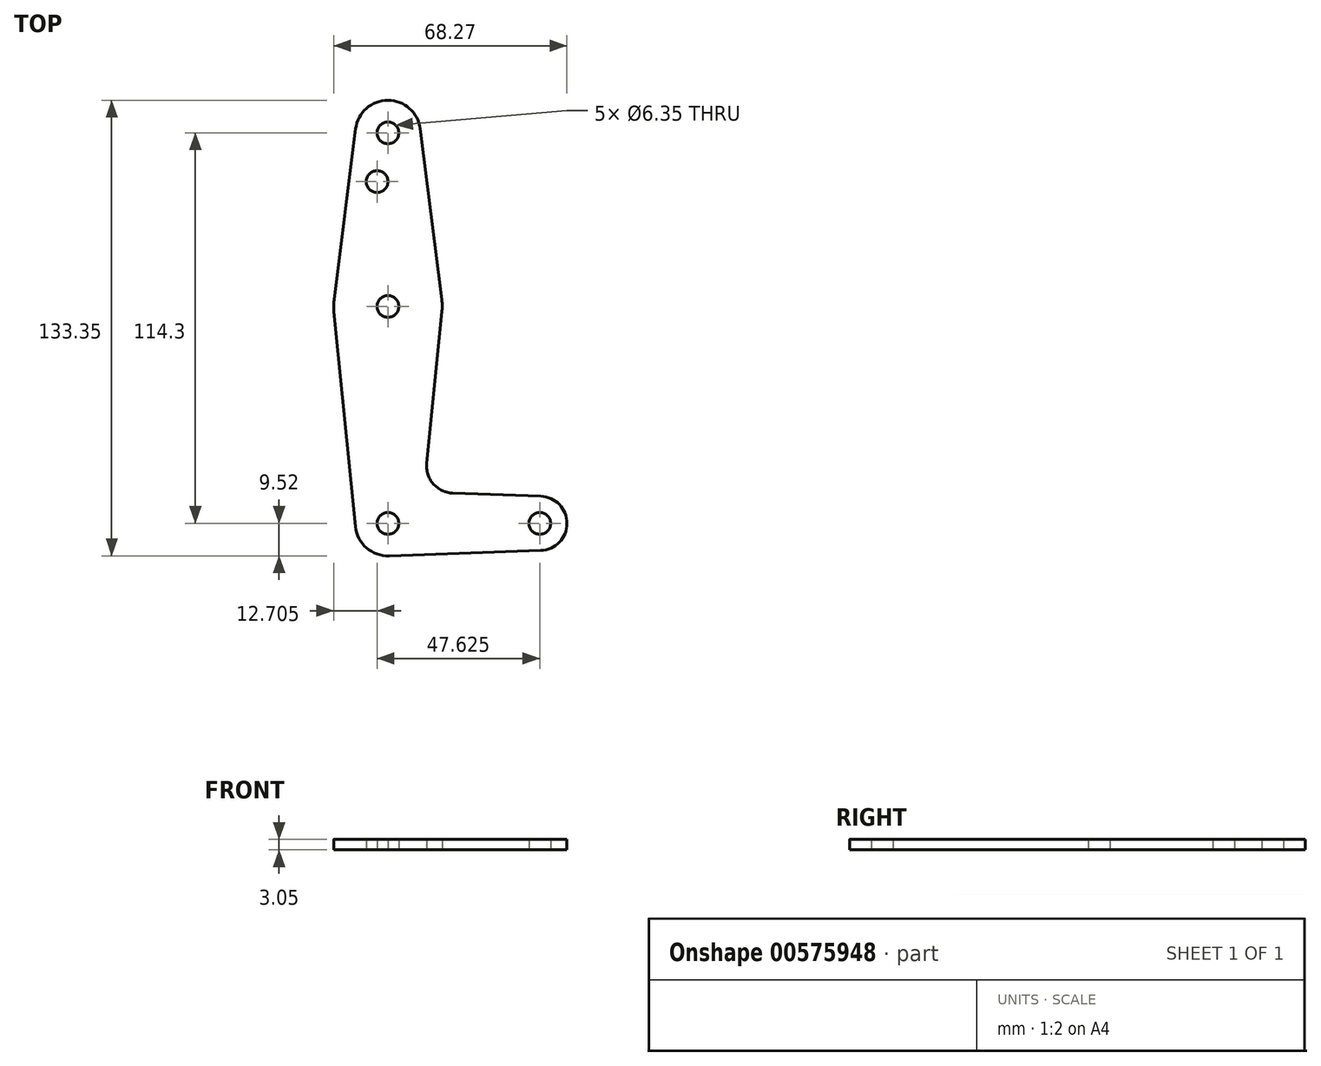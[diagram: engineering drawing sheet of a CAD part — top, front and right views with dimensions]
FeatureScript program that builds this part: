
annotation { "Feature Type Name" : "Feature", "Feature Type Description" : "" }
export const myFeature = defineFeature(function(context is Context, id is Id, definition is map)
    precondition{}
    {
        {
            var Q0;
            Q0=qCreatedBy(makeId("Top.planeOp"),FACE);
            var sketch = newSketch(context, id + "F0", { "sketchPlane" : qUnion([Q0])});
            skLineSegment(sketch, "E0", {"start": v(0, 0) * mm, "end": v(0, 114.3) * mm, "construction": true});
            skLineSegment(sketch, "E1", {"start": v(0, 0) * mm, "end": v(44.45, 0) * mm, "construction": true});
            skCircle(sketch, "E2", {"center": v(0, 114.3) * mm, "radius": 9.53 * mm});
            skCircle(sketch, "E3", {"center": v(0, 0) * mm, "radius": 9.53 * mm});
            skCircle(sketch, "E4", {"center": v(44.45, 0) * mm, "radius": 7.94 * mm});
            skCircle(sketch, "E5", {"center": v(0, 63.5) * mm, "radius": 15.88 * mm});
            skLineSegment(sketch, "E6", {"start": v(-15.75, 65.48) * mm, "end": v(-9.45, 115.5) * mm});
            skLineSegment(sketch, "E7", {"start": v(9.45, 115.5) * mm, "end": v(15.75, 65.48) * mm});
            skLineSegment(sketch, "E8", {"start": v(-15.8, 61.91) * mm, "end": v(-9.48, -0.95) * mm});
            skLineSegment(sketch, "E9", {"start": v(11.34, 17.6) * mm, "end": v(15.8, 61.91) * mm});
            skLineSegment(sketch, "E10", {"start": v(0.34, -9.52) * mm, "end": v(44.73, -7.93) * mm});
            skLineSegment(sketch, "E11", {"start": v(18.97, 8.85) * mm, "end": v(44.73, 7.93) * mm});
            skArc(sketch, "E12.filletArc", {"start": v(11.34, 17.6) * mm, "mid": v(13.26, 11.57) * mm, "end": v(18.97, 8.85) * mm});
            skCircle(sketch, "E13", {"center": v(0, 114.3) * mm, "radius": 3.18 * mm});
            skCircle(sketch, "E14", {"center": v(-3.18, 100.03) * mm, "radius": 3.18 * mm});
            skCircle(sketch, "E15", {"center": v(0, 63.5) * mm, "radius": 3.18 * mm});
            skCircle(sketch, "E16", {"center": v(0, 0) * mm, "radius": 3.18 * mm});
            skCircle(sketch, "E17", {"center": v(44.45, 0) * mm, "radius": 3.18 * mm});
            skSolve(sketch);
        }
        {
            var Q0;
            Q0 = qSketchRegion(id + "F0", true);
            extrude(context, id + "F1", {"entities" : qUnion([Q0]), "depth" : 3.05 * mm, "offsetDistance" : 25.4 * mm});
        }
    });
